# Revit family: 2M_Ball Valve_UNIVAL_BAV-0201 - 40-200 mm
name_source: partatom
category: Pipe Accessories
revit_build: Autodesk Revit 2016 (Build: 20150220_1215(x64)
units: mm (PartAtom-declared; Revit-internal decimal feet)

## family parameters
Always vertical = Yes
Cut with Voids When Loaded = No
OmniClass Number = 23.65.55.14.17
OmniClass Title = Adjusting/Controlling Valves for Liquid Services
Part Type = Valve - Breaks Into
Round Connector Dimension = Use Diameter
Shared = No
Work Plane-Based = No

## types (8) — shared parameters
Body Material = Cast iron
Certifications = TSE EAC CE
Connection Type = Flange
Description = Full port ball valve
Description TR = Tam geçişli küresel vana
Disc Material = Stainless steel
Gasket Material = PTFE
K Coefficient Table = Ball Valve Full Port Full Open
Loss Method = K Coefficient from Table
Manufacturer = Giacomini Unival
Giacomini Unival
Max. Working Pressure (Continious) = 6,7 bar for PN10 /11 bar for PN16
Max. Working Temperature = 120°
O-Ring Material = EPDM
PN10 = Yes
PN16 = Yes
Standard No = TS 3148
Stem Material = Stainless steel
URL = http://www.unival.com.tr

## per-type parameters (varying)
| type | Ball_D | D1 | DN | Flange | Flange_d | G | H | H1 | L | L1 | Model | Operator Type | Square_a |
| DN100 | 90 mm  [stored 0.295276 ft] | 70 mm  [stored 0.229659 ft] | 100 mm | M_Flange - 15-450 mm : DN100 | 17 mm | 335 mm | 170 mm  [stored 0.557743 ft] | 115 mm  [stored 0.377297 ft] | 190 mm | 78 mm  [stored 0.255906 ft] | BAV-0201X100 | M_Handle - Edged | 60 mm  [stored 0.19685 ft] |
| DN40 | 60 mm  [stored 0.19685 ft] | 40 mm  [stored 0.131234 ft] | 40 mm | M_Flange - 15-450 mm : DN40 | 17 mm | 190 mm | 120 mm  [stored 0.393701 ft] | 65 mm  [stored 0.213255 ft] | 140 mm  [stored 0.459318 ft] | 53 mm  [stored 0.173885 ft] | BAV-0201X040 | M_Handle - Edged | 55 mm  [stored 0.180446 ft] |
| DN50 | 65 mm  [stored 0.213255 ft] | 45 mm  [stored 0.147638 ft] | 50 mm | M_Flange - 15-450 mm : DN50 | 17 mm | 190 mm | 130 mm  [stored 0.426509 ft] | 75 mm | 150 mm  [stored 0.492126 ft] | 58 mm  [stored 0.190289 ft] | BAV-0201X050 | M_Handle - Edged | 55 mm  [stored 0.180446 ft] |
| DN65 | 73 mm  [stored 0.239501 ft] | 53 mm  [stored 0.173885 ft] | 65 mm | M_Flange - 15-450 mm : DN65 | 17 mm | 260 mm | 140 mm  [stored 0.459318 ft] | 85 mm  [stored 0.278871 ft] | 170 mm  [stored 0.557743 ft] | 68 mm  [stored 0.223097 ft] | BAV-0201X065 | M_Handle - Edged | 55 mm  [stored 0.180446 ft] |
| DN80 | 80 mm  [stored 0.262467 ft] | 60 mm  [stored 0.19685 ft] | 80 mm | M_Flange - 15-450 mm : DN80 | 17 mm | 335 mm | 155 mm  [stored 0.50853 ft] | 100 mm  [stored 0.328084 ft] | 180 mm | 73 mm  [stored 0.239501 ft] | BAV-0201X080 | M_Handle - Edged | 55 mm  [stored 0.180446 ft] |
| DN125 | 120 mm  [stored 0.393701 ft] | 83 mm  [stored 0.27231 ft] | 125 mm | M_Flange - 15-450 mm : DN125 | 17 mm | 335 mm | 190 mm | 135 mm | 325 mm | 146 mm | BAV-0201X125 | M_Handle - Edged | 65 mm  [stored 0.213255 ft] |
| DN150 | 140 mm  [stored 0.459318 ft] | 95 mm | 150 mm | M_Flange - 15-450 mm : DN150 | 17 mm | 700 mm | 245 mm | 190 mm | 350 mm | 158 mm | BAV-0201X150 | M_Handle - Straight | 90 mm  [stored 0.295276 ft] |
| DN200 | 172 mm | 120 mm  [stored 0.393701 ft] | 200 mm | M_Flange - 15-450 mm : DN200 | 18 mm  [stored 0.0590551 ft] | 700 mm | 280 mm | 225 mm | 400 mm | 182 mm | BAV-0201X200 | M_Handle - Straight | 90 mm  [stored 0.295276 ft] |

note: [stored X ft] marks values corroborated as IEEE doubles in the binary element streams (Revit-internal decimal feet)

## geometry (parser evidence)
native form markers: Sweep x8
no freeform markers — native parametric forms only
